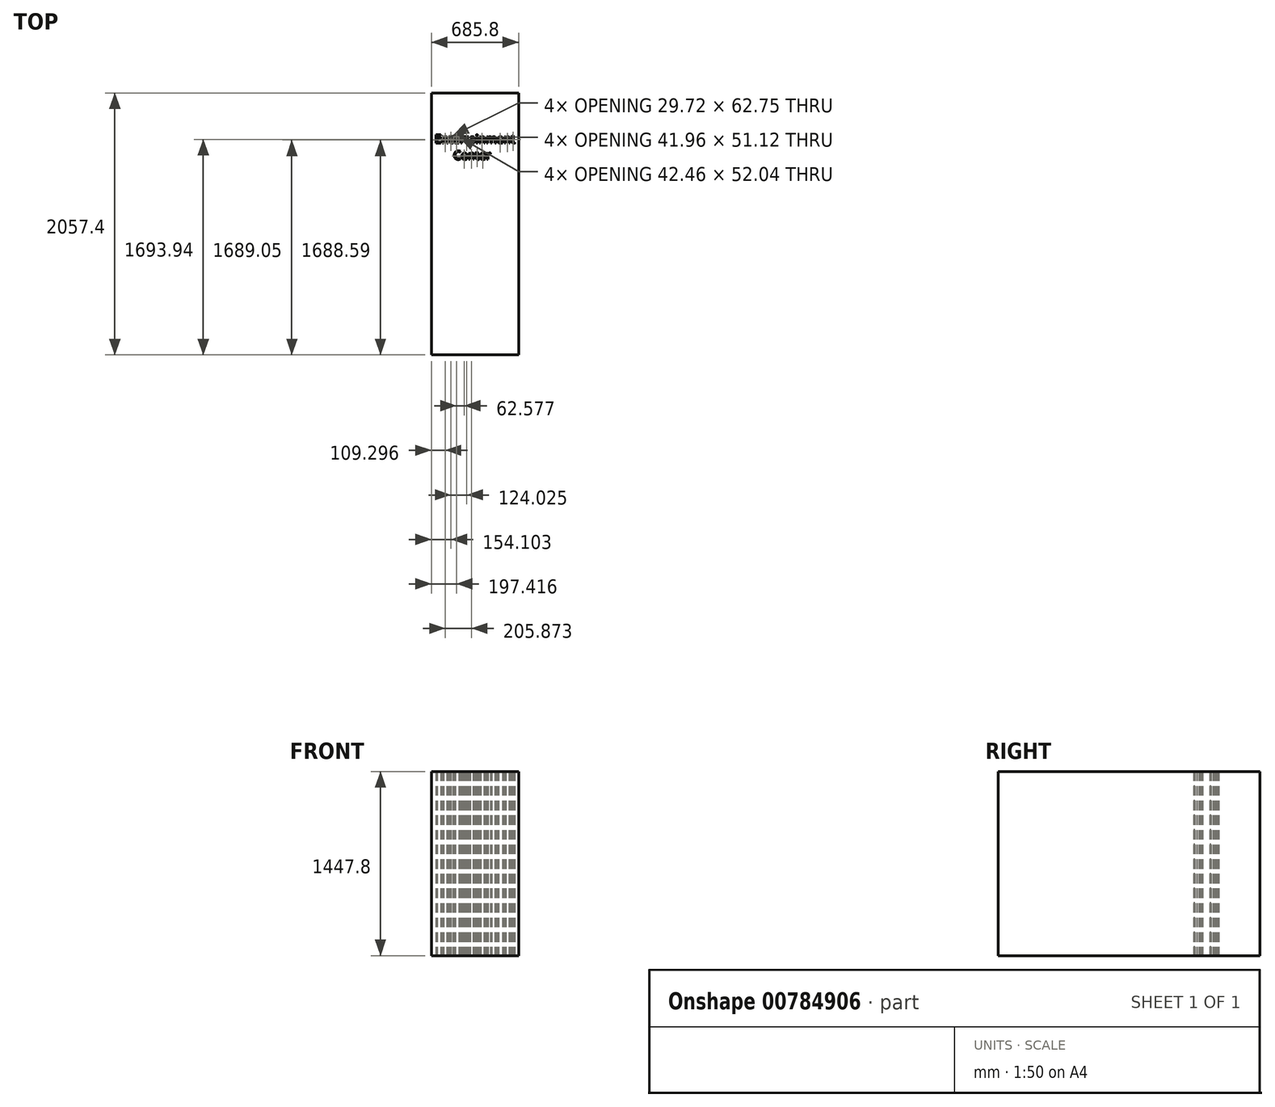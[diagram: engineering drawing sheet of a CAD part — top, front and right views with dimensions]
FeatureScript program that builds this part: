
annotation { "Feature Type Name" : "Feature", "Feature Type Description" : "" }
export const myFeature = defineFeature(function(context is Context, id is Id, definition is map)
    precondition{}
    {
        {
            var Q0;
            Q0=qCreatedBy(makeId("Top.planeOp"),FACE);
            var sketch = newSketch(context, id + "F0", { "sketchPlane" : qUnion([Q0])});
            skLineSegment(sketch, "E0.bottom", {"start": v(342.9, 1028.7) * mm, "end": v(-342.9, 1028.7) * mm});
            skLineSegment(sketch, "E0.top", {"start": v(342.9, -1028.7) * mm, "end": v(-342.9, -1028.7) * mm});
            skLineSegment(sketch, "E0.left", {"start": v(342.9, 1028.7) * mm, "end": v(342.9, -1028.7) * mm});
            skLineSegment(sketch, "E0.right", {"start": v(-342.9, 1028.7) * mm, "end": v(-342.9, -1028.7) * mm});
            skPoint(sketch, "E0.middle", {"position": v(0, 0) * mm});
            skText(sketch, "E1", { "text": "Entertainment\n      Center", "fontName": "OpenSans-Regular.ttf"});
            const initialGuessF0  = {"E1": [-0.3148, 0.63479, 1, 0, 0.06753]};
            skSetInitialGuess(sketch, initialGuessF0);
            skSolve(sketch);
        }
        {
            var Q0;
            Q0=makeQuery(id+"F0.imprint","IMPRINT",FACE,{"disambiguationData":[TD([[makeQuery(id+"F0.imprint","IMPRINT",EDGE,{"derivedFrom":sQuery(id+"F0.wireOp",EDGE,"E0.bottom")}),1.0]])]});
            extrude(context, id + "F1", {"entities" : qUnion([Q0]), "depth" : 1447.8 * mm, "offsetDistance" : 25.4 * mm});
        }
    });
